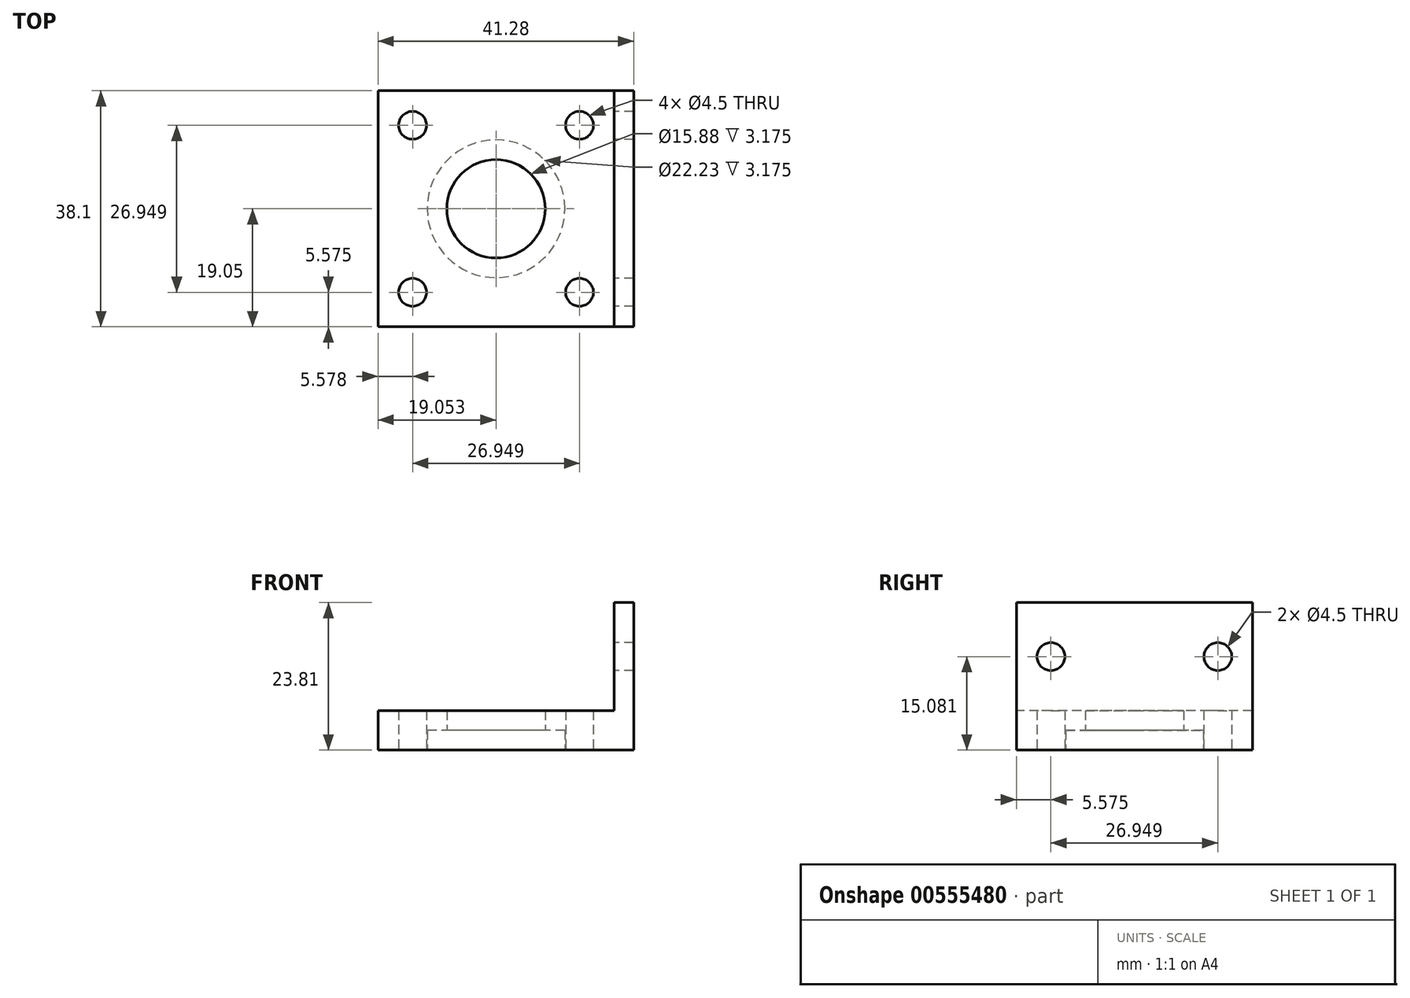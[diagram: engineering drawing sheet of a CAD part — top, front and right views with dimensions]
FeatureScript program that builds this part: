
annotation { "Feature Type Name" : "Feature", "Feature Type Description" : "" }
export const myFeature = defineFeature(function(context is Context, id is Id, definition is map)
    precondition{}
    {
        {
            var Q0;
            Q0=qCreatedBy(makeId("Top.planeOp"),FACE);
            var sketch = newSketch(context, id + "F0", { "sketchPlane" : qUnion([Q0])});
            skLineSegment(sketch, "E0.bottom", {"start": v(-20.64, 19.05) * mm, "end": v(20.64, 19.05) * mm});
            skLineSegment(sketch, "E0.top", {"start": v(-20.64, -19.05) * mm, "end": v(20.64, -19.05) * mm});
            skLineSegment(sketch, "E0.left", {"start": v(-20.64, 19.05) * mm, "end": v(-20.64, -19.05) * mm});
            skLineSegment(sketch, "E0.right", {"start": v(20.64, 19.05) * mm, "end": v(20.64, -19.05) * mm});
            skPoint(sketch, "E0.middle", {"position": v(0, 0) * mm});
            skLineSegment(sketch, "E1", {"start": v(17.46, 19.05) * mm, "end": v(17.46, -19.05) * mm});
            skLineSegment(sketch, "E2", {"start": v(-20.64, 13.47) * mm, "end": v(20.64, 13.47) * mm, "construction": true});
            skLineSegment(sketch, "E3", {"start": v(-15.06, 19.05) * mm, "end": v(-15.06, -19.05) * mm, "construction": true});
            skLineSegment(sketch, "E4", {"start": v(11.89, 19.05) * mm, "end": v(11.89, -19.05) * mm, "construction": true});
            skLineSegment(sketch, "E5", {"start": v(-20.64, -13.47) * mm, "end": v(20.64, -13.47) * mm, "construction": true});
            skLineSegment(sketch, "E6", {"start": v(-20.64, 0) * mm, "end": v(17.46, 0) * mm, "construction": true});
            skCircle(sketch, "E7", {"center": v(-1.59, 0) * mm, "radius": 11.11 * mm});
            skPoint(sketch, "E8", {"position": v(-15.06, -13.47) * mm});
            skPoint(sketch, "E9", {"position": v(-15.06, 13.47) * mm});
            skPoint(sketch, "E10", {"position": v(11.89, 13.47) * mm});
            skPoint(sketch, "E11", {"position": v(11.89, -13.47) * mm});
            skCircle(sketch, "E12", {"center": v(-1.59, 0) * mm, "radius": 7.94 * mm});
            skSolve(sketch);
        }
        {
            var Q0;
            {var subQ0=sQuery(id+"F0.wireOp",EDGE,"E0.right");Q0=makeQuery(id+"F0.imprint","IMPRINT",FACE,{"disambiguationData":[TD([[makeQuery(id+"F0.imprint","IMPRINT",EDGE,{"derivedFrom":subQ0}),-1.0]])]});}
            extrude(context, id + "F1", {"entities" : qUnion([Q0]), "depth" : 23.8 * mm, "offsetDistance" : 25.4 * mm});
        }
        {
            var Q0;
            {var subQ1=sQuery(id+"F0.wireOp",EDGE,"E0.left");Q0=makeQuery(id+"F0.imprint","IMPRINT",FACE,{"disambiguationData":[TD([[makeQuery(id+"F0.imprint","IMPRINT",EDGE,{"derivedFrom":subQ1}),1.0]])]});}
            var Q1;
            Q1=makeQuery(id+"F0.imprint","IMPRINT",FACE,{"disambiguationData":[TD([[makeQuery(id+"F0.imprint","IMPRINT",EDGE,{"derivedFrom":sQuery(id+"F0.wireOp",EDGE,"E7")}),1.0]])]});
            extrude(context, id + "F2", {"entities" : qUnion([Q0, Q1]), "operationType" : NewBodyOperationType.ADD, "depth" : 6.35 * mm, "offsetDistance" : 25.4 * mm});
        }
        {
            var Q0;
            Q0=makeQuery(id+"F1.opExtrude","SWEPT_FACE",FACE,{"disambiguationData":[OSD([sQuery(id+"F0.wireOp",EDGE,"E1")])]});
            var sketch = newSketch(context, id + "F3", { "sketchPlane" : qUnion([Q0])});
            skPoint(sketch, "E13.endSnap0", {"position": v(-19.05, 15.08) * mm});
            skLineSegment(sketch, "E14", {"start": v(0, 23.81) * mm, "end": v(0, 6.35) * mm, "construction": true});
            skPoint(sketch, "E15", {"position": v(0, 15.08) * mm});
            skLineSegment(sketch, "E16", {"start": v(-19.05, 15.08) * mm, "end": v(19.05, 15.08) * mm, "construction": true});
            skPoint(sketch, "E17", {"position": v(-13.47, 15.08) * mm});
            skPoint(sketch, "E18", {"position": v(13.47, 15.08) * mm});
            skSolve(sketch);
        }
        {
            var Q0;
            Q0=sQuery(id+"F0.wireOp",VERTEX,"E8");
            var Q1;
            Q1=makeQuery(id+"F1.opExtrude","SWEPT_BODY",BODY,{"disambiguationData":[OSD([sQuery(id+"F0.wireOp",EDGE,"E0.bottom"),sQuery(id+"F0.wireOp",EDGE,"E0.top"),sQuery(id+"F0.wireOp",EDGE,"E0.right"),sQuery(id+"F0.wireOp",EDGE,"E1")])]});
            hole(context, id + "F4", {"style" : HoleStyle.SIMPLE, "endStyle" : HoleEndStyle.THROUGH, "oppositeDirection" : true, "standardTappedOrClearance" : lookupTablePath({ "standard" : "ANSI", "fit" : "Normal (ASME)", "size" : "#8", "type" : "Clearance" }), "standardBlindInLast" : lookupTablePath({ "fit" : "Free", "standard" : "ANSI", "size" : "#8", "type" : "Clearance" }), "holeDiameter" : 4.5 * mm, "isTappedThrough" : true, "tappedDepth" : 12.7 * mm, "tapClearance" : 3, "locations" : qUnion([Q0]), "scope" : qUnion([Q1])});
        }
        {
            var Q0;
            Q0=sQuery(id+"F0.wireOp",VERTEX,"E9");
            var Q1;
            Q1=makeQuery(id+"F1.opExtrude","SWEPT_BODY",BODY,{"disambiguationData":[OSD([sQuery(id+"F0.wireOp",EDGE,"E0.bottom"),sQuery(id+"F0.wireOp",EDGE,"E0.top"),sQuery(id+"F0.wireOp",EDGE,"E0.right"),sQuery(id+"F0.wireOp",EDGE,"E1")])]});
            hole(context, id + "F5", {"style" : HoleStyle.SIMPLE, "endStyle" : HoleEndStyle.THROUGH, "oppositeDirection" : true, "standardTappedOrClearance" : lookupTablePath({ "standard" : "ANSI", "fit" : "Normal (ASME)", "size" : "#8", "type" : "Clearance" }), "standardBlindInLast" : lookupTablePath({ "fit" : "Free", "standard" : "ANSI", "size" : "#8", "type" : "Clearance" }), "holeDiameter" : 4.5 * mm, "isTappedThrough" : true, "tappedDepth" : 12.7 * mm, "tapClearance" : 3, "locations" : qUnion([Q0]), "scope" : qUnion([Q1])});
        }
        {
            var Q0;
            Q0=sQuery(id+"F0.wireOp",VERTEX,"E10");
            var Q1;
            Q1=makeQuery(id+"F1.opExtrude","SWEPT_BODY",BODY,{"disambiguationData":[OSD([sQuery(id+"F0.wireOp",EDGE,"E0.bottom"),sQuery(id+"F0.wireOp",EDGE,"E0.top"),sQuery(id+"F0.wireOp",EDGE,"E0.right"),sQuery(id+"F0.wireOp",EDGE,"E1")])]});
            hole(context, id + "F6", {"style" : HoleStyle.SIMPLE, "endStyle" : HoleEndStyle.THROUGH, "oppositeDirection" : true, "standardTappedOrClearance" : lookupTablePath({ "standard" : "ANSI", "fit" : "Normal (ASME)", "size" : "#8", "type" : "Clearance" }), "standardBlindInLast" : lookupTablePath({ "fit" : "Free", "standard" : "ANSI", "size" : "#8", "type" : "Clearance" }), "holeDiameter" : 4.5 * mm, "isTappedThrough" : true, "tappedDepth" : 12.7 * mm, "tapClearance" : 3, "locations" : qUnion([Q0]), "scope" : qUnion([Q1])});
        }
        {
            var Q0;
            Q0=sQuery(id+"F0.wireOp",VERTEX,"E11");
            var Q1;
            Q1=makeQuery(id+"F1.opExtrude","SWEPT_BODY",BODY,{"disambiguationData":[OSD([sQuery(id+"F0.wireOp",EDGE,"E0.bottom"),sQuery(id+"F0.wireOp",EDGE,"E0.top"),sQuery(id+"F0.wireOp",EDGE,"E0.right"),sQuery(id+"F0.wireOp",EDGE,"E1")])]});
            hole(context, id + "F7", {"style" : HoleStyle.SIMPLE, "endStyle" : HoleEndStyle.THROUGH, "oppositeDirection" : true, "standardTappedOrClearance" : lookupTablePath({ "standard" : "ANSI", "fit" : "Normal (ASME)", "size" : "#8", "type" : "Clearance" }), "standardBlindInLast" : lookupTablePath({ "fit" : "Free", "standard" : "ANSI", "size" : "#8", "type" : "Clearance" }), "holeDiameter" : 4.5 * mm, "isTappedThrough" : true, "tappedDepth" : 12.7 * mm, "tapClearance" : 3, "locations" : qUnion([Q0]), "scope" : qUnion([Q1])});
        }
        {
            var Q0;
            Q0=sQuery(id+"F3.wireOp",VERTEX,"E17");
            var Q1;
            Q1=makeQuery(id+"F1.opExtrude","SWEPT_BODY",BODY,{"disambiguationData":[OSD([sQuery(id+"F0.wireOp",EDGE,"E0.bottom"),sQuery(id+"F0.wireOp",EDGE,"E0.top"),sQuery(id+"F0.wireOp",EDGE,"E0.right"),sQuery(id+"F0.wireOp",EDGE,"E1")])]});
            hole(context, id + "F8", {"style" : HoleStyle.SIMPLE, "endStyle" : HoleEndStyle.THROUGH, "standardTappedOrClearance" : lookupTablePath({ "standard" : "ANSI", "fit" : "Normal (ASME)", "size" : "#8", "type" : "Clearance" }), "standardBlindInLast" : lookupTablePath({ "fit" : "Free", "standard" : "ANSI", "size" : "#8", "type" : "Clearance" }), "holeDiameter" : 4.5 * mm, "isTappedThrough" : true, "tappedDepth" : 12.7 * mm, "tapClearance" : 3, "locations" : qUnion([Q0]), "scope" : qUnion([Q1])});
        }
        {
            var Q0;
            Q0=sQuery(id+"F3.wireOp",VERTEX,"E18");
            var Q1;
            Q1=makeQuery(id+"F1.opExtrude","SWEPT_BODY",BODY,{"disambiguationData":[OSD([sQuery(id+"F0.wireOp",EDGE,"E0.bottom"),sQuery(id+"F0.wireOp",EDGE,"E0.top"),sQuery(id+"F0.wireOp",EDGE,"E0.right"),sQuery(id+"F0.wireOp",EDGE,"E1")])]});
            hole(context, id + "F9", {"style" : HoleStyle.SIMPLE, "endStyle" : HoleEndStyle.THROUGH, "standardTappedOrClearance" : lookupTablePath({ "standard" : "ANSI", "fit" : "Normal (ASME)", "size" : "#8", "type" : "Clearance" }), "standardBlindInLast" : lookupTablePath({ "fit" : "Free", "standard" : "ANSI", "size" : "#8", "type" : "Clearance" }), "holeDiameter" : 4.5 * mm, "isTappedThrough" : true, "tappedDepth" : 12.7 * mm, "tapClearance" : 3, "locations" : qUnion([Q0]), "scope" : qUnion([Q1])});
        }
        {
            var Q0;
            Q0=makeQuery(id+"F0.imprint","IMPRINT",FACE,{"disambiguationData":[TD([[makeQuery(id+"F0.imprint","IMPRINT",EDGE,{"derivedFrom":sQuery(id+"F0.wireOp",EDGE,"E7")}),1.0]])]});
            extrude(context, id + "F10", {"entities" : qUnion([Q0]), "operationType" : NewBodyOperationType.REMOVE, "depth" : 3.17 * mm, "offsetDistance" : 25.4 * mm});
        }
    });
